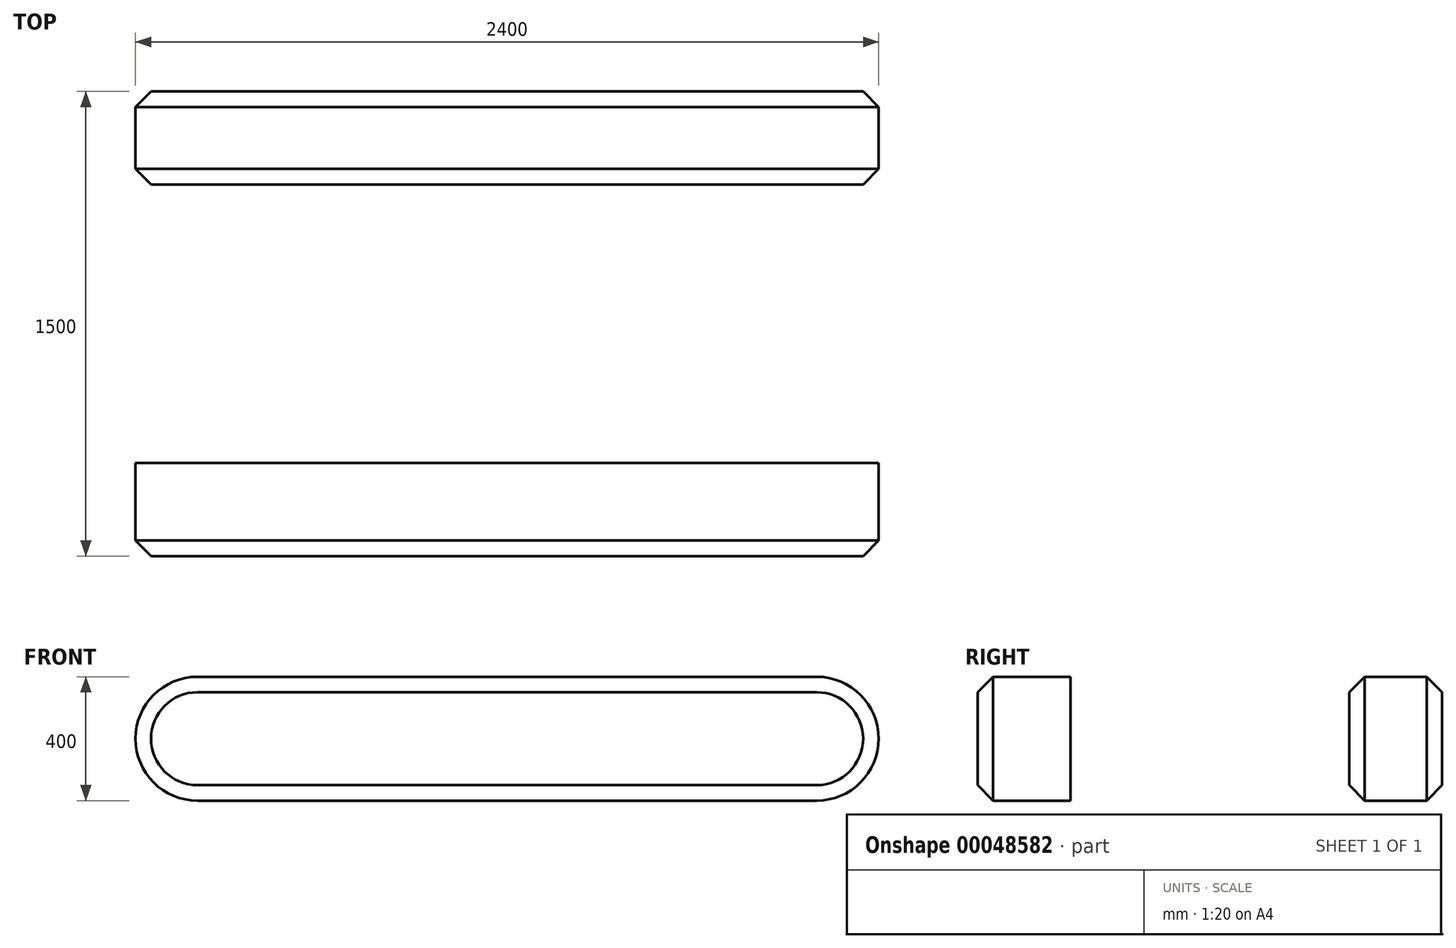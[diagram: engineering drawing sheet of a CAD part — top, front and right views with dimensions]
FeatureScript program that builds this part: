
annotation { "Feature Type Name" : "Feature", "Feature Type Description" : "" }
export const myFeature = defineFeature(function(context is Context, id is Id, definition is map)
    precondition{}
    {
        {
            var Q0;
            Q0=qCreatedBy(makeId("Front.planeOp"),FACE);
            var sketch = newSketch(context, id + "F0", { "sketchPlane" : qUnion([Q0])});
            skArc(sketch, "E0", {"start": v(-1000, 200) * mm, "mid": v(-1200, 0) * mm, "end": v(-1000, -200) * mm});
            skArc(sketch, "E1.MirrorC", {"start": v(1000, 200) * mm, "mid": v(1200, 0) * mm, "end": v(1000, -200) * mm});
            skLineSegment(sketch, "E2", {"start": v(-1000, 200) * mm, "end": v(1000, 200) * mm});
            skLineSegment(sketch, "E3", {"start": v(-1000, -200) * mm, "end": v(1000, -200) * mm});
            skSolve(sketch);
        }
        {
            var Q0;
            Q0=makeQuery(id+"F0.imprint","IMPRINT",FACE,{"disambiguationData":[TD([[makeQuery(id+"F0.imprint","IMPRINT",EDGE,{"derivedFrom":sQuery(id+"F0.wireOp",EDGE,"E0")}),1.0]])]});
            extrude(context, id + "F1", {"entities" : qUnion([Q0]), "endBound" : BoundingType.SYMMETRIC, "depth" : 1500 * mm});
        }
        {
            var Q0;
            Q0 = qSketchRegion(id + "F0", true);
            extrude(context, id + "F2", {"entities" : qUnion([Q0]), "operationType" : NewBodyOperationType.REMOVE, "endBound" : BoundingType.SYMMETRIC, "oppositeDirection" : true, "depth" : 900 * mm});
        }
        {
            var Q0;
            Q0=makeQuery(id+"F1.opExtrude","CAP_EDGE",EDGE,{"disambiguationData":[OSD([sQuery(id+"F0.wireOp",EDGE,"E2")])],"isStart":false});
            var Q1;
            Q1=makeQuery(id+"F1.opExtrude","CAP_EDGE",EDGE,{"disambiguationData":[OSD([sQuery(id+"F0.wireOp",EDGE,"E0")])],"isStart":false});
            var Q2;
            Q2=makeQuery(id+"F1.opExtrude","CAP_EDGE",EDGE,{"disambiguationData":[OSD([sQuery(id+"F0.wireOp",EDGE,"E3")])],"isStart":false});
            var Q3;
            Q3=makeQuery(id+"F1.opExtrude","CAP_EDGE",EDGE,{"disambiguationData":[OSD([sQuery(id+"F0.wireOp",EDGE,"E1.MirrorC")])],"isStart":false});
            var Q4;
            Q4=makeQuery(id+"F2.boolean.opBoolean","COPY",EDGE,{"derivedFrom":makeQuery(id+"F2.opExtrude","CAP_EDGE",EDGE,{"disambiguationData":[OSD([sQuery(id+"F0.wireOp",EDGE,"E2")])],"isStart":true})});
            var Q5;
            Q5=makeQuery(id+"F1.opExtrude","CAP_EDGE",EDGE,{"disambiguationData":[OSD([sQuery(id+"F0.wireOp",EDGE,"E2")])],"isStart":true});
            var Q6;
            Q6=makeQuery(id+"F2.boolean.opBoolean","COPY",EDGE,{"derivedFrom":makeQuery(id+"F2.opExtrude","CAP_EDGE",EDGE,{"disambiguationData":[OSD([sQuery(id+"F0.wireOp",EDGE,"E2")])],"isStart":false})});
            chamfer(context, id + "F3", {"entities" : qUnion([Q0, Q1, Q2, Q3, Q4, Q5, Q6]), "width" : 50 * mm, "tangentPropagation" : true});
        }
    });
